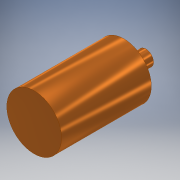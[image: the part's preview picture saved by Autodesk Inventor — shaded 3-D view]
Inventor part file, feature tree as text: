
AUTODESK INVENTOR PART (.ipt)
format: ipt  version: 2018 (Build 220112000, 112)  size: 105,472 bytes
history: native  units: mm
features: extrude x2, sketch x2
ambient origin geometry x8: Origin, YZ Plane, XZ Plane, XY Plane, X Axis, Y Axis, Z Axis, Center Point
bodies: 实体1 (feature_tree)
feature tree (4):
  extrude  "拉伸1"  Depth=41.0mm TaperAngle=0.0deg
  extrude  "拉伸2"  Depth=10.0mm TaperAngle=0.0deg
  sketch  "草图1"  dims[d0=25.0mm d1=41.0mm d2=0.0mm]
  sketch  "草图2"  dims[d3=7.0mm d4=10.0mm d5=0.0mm]
